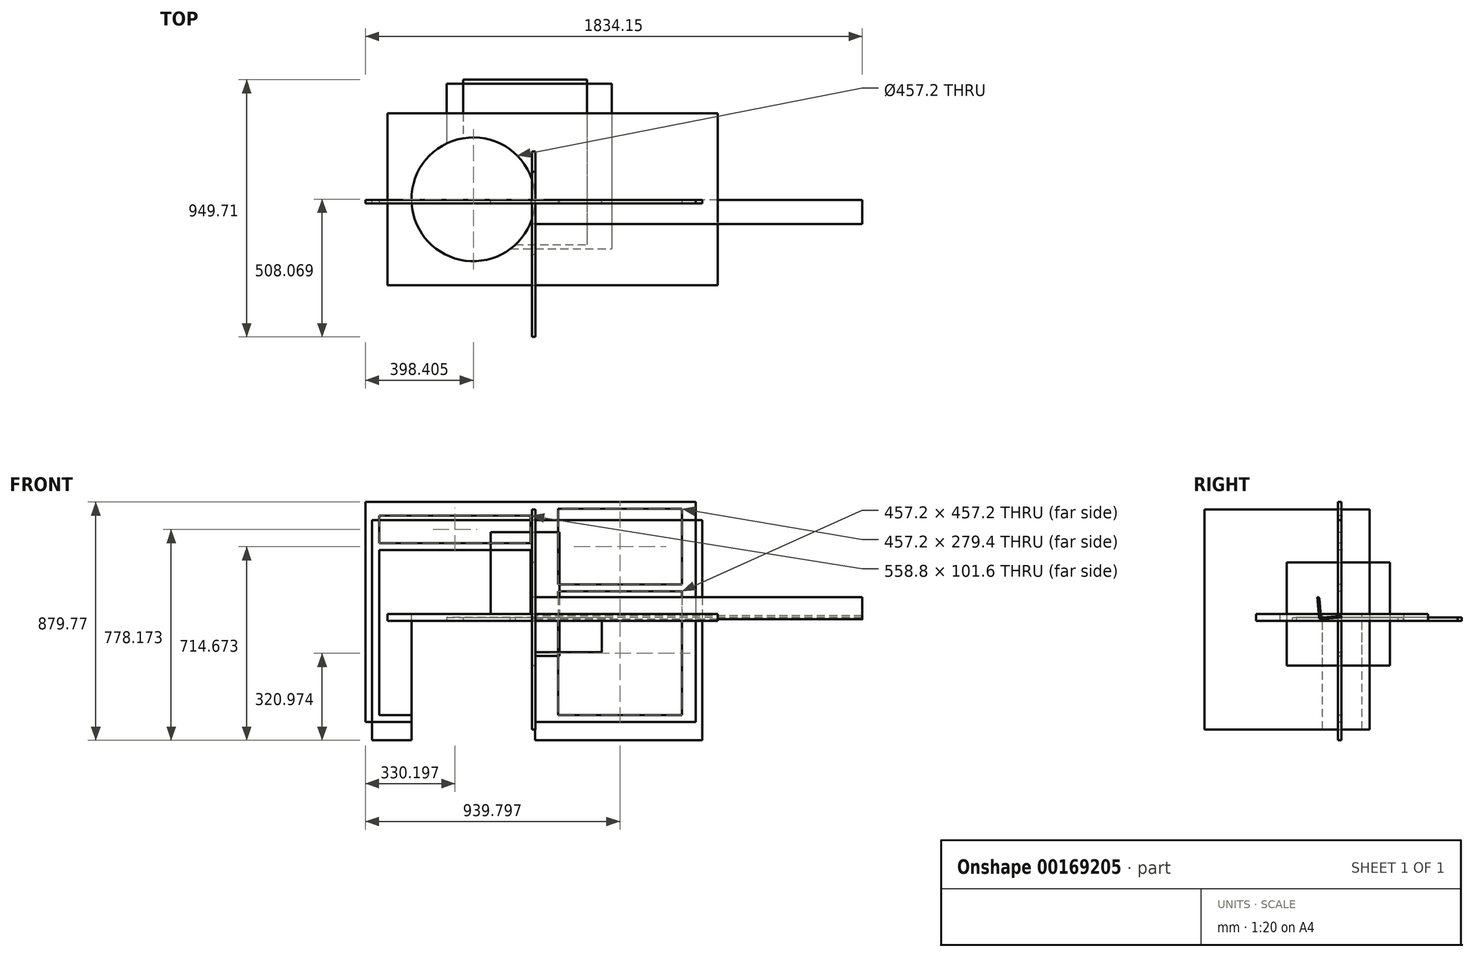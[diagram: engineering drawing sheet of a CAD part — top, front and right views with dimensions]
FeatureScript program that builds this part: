
annotation { "Feature Type Name" : "Feature", "Feature Type Description" : "" }
export const myFeature = defineFeature(function(context is Context, id is Id, definition is map)
    precondition{}
    {
        {
            var Q0;
            Q0=qCreatedBy(makeId("Front.planeOp"),FACE);
            var sketch = newSketch(context, id + "F0", { "sketchPlane" : qUnion([Q0])});
            skLineSegment(sketch, "E0.bottom", {"start": v(-614.95, 439.21) * mm, "end": v(604.25, 439.21) * mm});
            skLineSegment(sketch, "E0.top", {"start": v(-614.95, -373.59) * mm, "end": v(604.25, -373.59) * mm});
            skLineSegment(sketch, "E0.left", {"start": v(-614.95, 439.21) * mm, "end": v(-614.95, -373.59) * mm});
            skLineSegment(sketch, "E0.right", {"start": v(604.25, 439.21) * mm, "end": v(604.25, -373.59) * mm});
            skSolve(sketch);
        }
        {
            var Q0;
            Q0 = qSketchRegion(id + "F0", true);
            extrude(context, id + "F1", {"entities" : qUnion([Q0]), "depth" : 12.7 * mm});
        }
        {
            var Q0;
            Q0=makeQuery(id+"F1.opExtrude","CAP_FACE",FACE,{"disambiguationData":[OSD([sQuery(id+"F0.wireOp",EDGE,"E0.bottom"),sQuery(id+"F0.wireOp",EDGE,"E0.top"),sQuery(id+"F0.wireOp",EDGE,"E0.left"),sQuery(id+"F0.wireOp",EDGE,"E0.right")])],"isStart":false});
            var sketch = newSketch(context, id + "F2", { "sketchPlane" : qUnion([Q0])});
            skLineSegment(sketch, "E1.bottom", {"start": v(-564.15, 261.41) * mm, "end": v(-5.35, 261.41) * mm});
            skLineSegment(sketch, "E1.top", {"start": v(-564.15, -348.19) * mm, "end": v(-5.35, -348.19) * mm});
            skLineSegment(sketch, "E1.left", {"start": v(-564.15, 261.41) * mm, "end": v(-564.15, -348.19) * mm});
            skLineSegment(sketch, "E1.right", {"start": v(-5.35, 261.41) * mm, "end": v(-5.35, -348.19) * mm});
            skLineSegment(sketch, "E2.bottom", {"start": v(96.25, 109.01) * mm, "end": v(553.45, 109.01) * mm});
            skLineSegment(sketch, "E2.top", {"start": v(96.25, -348.19) * mm, "end": v(553.45, -348.19) * mm});
            skLineSegment(sketch, "E2.left", {"start": v(96.25, 109.01) * mm, "end": v(96.25, -348.19) * mm});
            skLineSegment(sketch, "E2.right", {"start": v(553.45, 109.01) * mm, "end": v(553.45, -348.19) * mm});
            skLineSegment(sketch, "E3.bottom", {"start": v(96.25, 413.81) * mm, "end": v(553.45, 413.81) * mm});
            skLineSegment(sketch, "E3.top", {"start": v(96.25, 134.41) * mm, "end": v(553.45, 134.41) * mm});
            skLineSegment(sketch, "E3.left", {"start": v(96.25, 413.81) * mm, "end": v(96.25, 134.41) * mm});
            skLineSegment(sketch, "E3.right", {"start": v(553.45, 413.81) * mm, "end": v(553.45, 134.41) * mm});
            skLineSegment(sketch, "E4.bottom", {"start": v(-564.15, 388.41) * mm, "end": v(-5.35, 388.41) * mm});
            skLineSegment(sketch, "E4.top", {"start": v(-564.15, 286.81) * mm, "end": v(-5.35, 286.81) * mm});
            skLineSegment(sketch, "E4.left", {"start": v(-564.15, 388.41) * mm, "end": v(-564.15, 286.81) * mm});
            skLineSegment(sketch, "E4.right", {"start": v(-5.35, 388.41) * mm, "end": v(-5.35, 286.81) * mm});
            skSolve(sketch);
        }
        {
            var Q0;
            Q0 = qSketchRegion(id + "F2", true);
            extrude(context, id + "F3", {"entities" : qUnion([Q0]), "operationType" : NewBodyOperationType.REMOVE, "endBound" : BoundingType.THROUGH_ALL, "oppositeDirection" : true, "depth" : 25.4 * mm});
        }
        {
            var Q0;
            Q0=qCreatedBy(makeId("Right.planeOp"),FACE);
            var sketch = newSketch(context, id + "F4", { "sketchPlane" : qUnion([Q0])});
            skLineSegment(sketch, "E5.bottom", {"start": v(-505.32, 412.33) * mm, "end": v(104.28, 412.33) * mm});
            skLineSegment(sketch, "E5.top", {"start": v(-505.32, -400.47) * mm, "end": v(104.28, -400.47) * mm});
            skLineSegment(sketch, "E5.left", {"start": v(-505.32, 412.33) * mm, "end": v(-505.32, -400.47) * mm});
            skLineSegment(sketch, "E5.right", {"start": v(104.28, 412.33) * mm, "end": v(104.28, -400.47) * mm});
            skSolve(sketch);
        }
        {
            var Q0;
            Q0 = qSketchRegion(id + "F4", true);
            extrude(context, id + "F5", {"entities" : qUnion([Q0]), "depth" : 12.7 * mm});
        }
        {
            var Q0;
            Q0=qCreatedBy(makeId("Front.planeOp"),FACE);
            var sketch = newSketch(context, id + "F6", { "sketchPlane" : qUnion([Q0])});
            skLineSegment(sketch, "E6.bottom", {"start": v(628.26, 372.24) * mm, "end": v(-590.94, 372.24) * mm});
            skLineSegment(sketch, "E6.top", {"start": v(628.26, -440.56) * mm, "end": v(-590.94, -440.56) * mm});
            skLineSegment(sketch, "E6.left", {"start": v(628.26, 372.24) * mm, "end": v(628.26, -440.56) * mm});
            skLineSegment(sketch, "E6.right", {"start": v(-590.94, 372.24) * mm, "end": v(-590.94, -440.56) * mm});
            skSolve(sketch);
        }
        {
            var Q0;
            Q0 = qSketchRegion(id + "F6", true);
            extrude(context, id + "F7", {"entities" : qUnion([Q0]), "depth" : 12.7 * mm});
        }
        {
            var Q0;
            Q0=qCreatedBy(makeId("Top.planeOp"),FACE);
            var sketch = newSketch(context, id + "F8", { "sketchPlane" : qUnion([Q0])});
            skLineSegment(sketch, "E7.bottom", {"start": v(-534.05, 320.25) * mm, "end": v(685.15, 320.25) * mm});
            skLineSegment(sketch, "E7.top", {"start": v(-534.05, -314.75) * mm, "end": v(685.15, -314.75) * mm});
            skLineSegment(sketch, "E7.left", {"start": v(-534.05, 320.25) * mm, "end": v(-534.05, -314.75) * mm});
            skLineSegment(sketch, "E7.right", {"start": v(685.15, 320.25) * mm, "end": v(685.15, -314.75) * mm});
            skSolve(sketch);
        }
        {
            var Q0;
            Q0 = qSketchRegion(id + "F8", true);
            extrude(context, id + "F9", {"entities" : qUnion([Q0]), "depth" : 25.4 * mm});
        }
        {
            var Q0;
            Q0=qCreatedBy(makeId("Top.planeOp"),FACE);
            var sketch = newSketch(context, id + "F10", { "sketchPlane" : qUnion([Q0])});
            skLineSegment(sketch, "E8.bottom", {"start": v(-315.36, 429.37) * mm, "end": v(294.24, 429.37) * mm});
            skLineSegment(sketch, "E8.top", {"start": v(-315.36, -180.23) * mm, "end": v(294.24, -180.23) * mm});
            skLineSegment(sketch, "E8.left", {"start": v(-315.36, 429.37) * mm, "end": v(-315.36, -180.23) * mm});
            skLineSegment(sketch, "E8.right", {"start": v(294.24, 429.37) * mm, "end": v(294.24, -180.23) * mm});
            skSolve(sketch);
        }
        {
            var Q0;
            Q0 = qSketchRegion(id + "F10", true);
            extrude(context, id + "F11", {"entities" : qUnion([Q0]), "depth" : 12.7 * mm});
        }
        {
            var Q0;
            Q0=qCreatedBy(makeId("Top.planeOp"),FACE);
            var sketch = newSketch(context, id + "F12", { "sketchPlane" : qUnion([Q0])});
            skLineSegment(sketch, "E9.bottom", {"start": v(-254.5, 444.4) * mm, "end": v(202.7, 444.4) * mm});
            skLineSegment(sketch, "E9.top", {"start": v(-254.5, -165.2) * mm, "end": v(202.7, -165.2) * mm});
            skLineSegment(sketch, "E9.left", {"start": v(-254.5, 444.4) * mm, "end": v(-254.5, -165.2) * mm});
            skLineSegment(sketch, "E9.right", {"start": v(202.7, 444.4) * mm, "end": v(202.7, -165.2) * mm});
            skSolve(sketch);
        }
        {
            var Q0;
            Q0 = qSketchRegion(id + "F12", true);
            extrude(context, id + "F13", {"entities" : qUnion([Q0]), "depth" : 12.7 * mm});
        }
        {
            var Q0;
            Q0=qCreatedBy(makeId("Front.planeOp"),FACE);
            var sketch = newSketch(context, id + "F14", { "sketchPlane" : qUnion([Q0])});
            skLineSegment(sketch, "E10.bottom", {"start": v(-326.1, 12.28) * mm, "end": v(258.1, 12.28) * mm});
            skLineSegment(sketch, "E10.top", {"start": v(-326.1, -114.72) * mm, "end": v(258.1, -114.72) * mm});
            skLineSegment(sketch, "E10.left", {"start": v(-326.1, 12.28) * mm, "end": v(-326.1, -114.72) * mm});
            skLineSegment(sketch, "E10.right", {"start": v(258.1, 12.28) * mm, "end": v(258.1, -114.72) * mm});
            skSolve(sketch);
        }
        {
            var Q0;
            Q0 = qSketchRegion(id + "F14", true);
            extrude(context, id + "F15", {"entities" : qUnion([Q0]), "depth" : 12.7 * mm});
        }
        {
            var Q0;
            Q0=qCreatedBy(makeId("Front.planeOp"),FACE);
            var sketch = newSketch(context, id + "F16", { "sketchPlane" : qUnion([Q0])});
            skLineSegment(sketch, "E11.bottom", {"start": v(-152.62, 328.2) * mm, "end": v(101.38, 328.2) * mm});
            skLineSegment(sketch, "E11.top", {"start": v(-152.62, -129) * mm, "end": v(101.38, -129) * mm});
            skLineSegment(sketch, "E11.left", {"start": v(-152.62, 328.2) * mm, "end": v(-152.62, -129) * mm});
            skLineSegment(sketch, "E11.right", {"start": v(101.38, 328.2) * mm, "end": v(101.38, -129) * mm});
            skSolve(sketch);
        }
        {
            var Q0;
            Q0 = qSketchRegion(id + "F16", true);
            extrude(context, id + "F17", {"entities" : qUnion([Q0]), "depth" : 12.7 * mm});
        }
        {
            var Q0;
            Q0=qCreatedBy(makeId("Right.planeOp"),FACE);
            var sketch = newSketch(context, id + "F18", { "sketchPlane" : qUnion([Q0])});
            skLineSegment(sketch, "E12", {"start": v(-81.89, 82.36) * mm, "end": v(-76.46, 19.1) * mm});
            skLineSegment(sketch, "E13", {"start": v(-69.6, 13.3) * mm, "end": v(-6.33, 18.73) * mm});
            skLineSegment(sketch, "E14.0", {"start": v(-75.38, 6.44) * mm, "end": v(0.54, 12.95) * mm});
            skLineSegment(sketch, "E14.1", {"start": v(-88.76, 88.15) * mm, "end": v(-82.25, 12.22) * mm});
            skLineSegment(sketch, "E15", {"start": v(-88.76, 88.15) * mm, "end": v(-88.76, 88.15) * mm});
            skLineSegment(sketch, "E16", {"start": v(0.54, 12.95) * mm, "end": v(0.54, 12.95) * mm});
            skPoint(sketch, "E17.visualSharp", {"position": v(-75.92, 12.77) * mm});
            skArc(sketch, "E17.filletArc", {"start": v(-76.46, 19.1) * mm, "mid": v(-74.23, 14.78) * mm, "end": v(-69.6, 13.3) * mm});
            skPoint(sketch, "E18.visualSharp", {"position": v(-81.7, 5.9) * mm});
            skArc(sketch, "E18.filletArc", {"start": v(-82.25, 12.22) * mm, "mid": v(-80.01, 7.91) * mm, "end": v(-75.38, 6.44) * mm});
            skPoint(sketch, "E19.visualSharp", {"position": v(0, 19.27) * mm});
            skArc(sketch, "E19.filletArc", {"start": v(0.54, 12.95) * mm, "mid": v(-1.7, 17.26) * mm, "end": v(-6.33, 18.73) * mm});
            skPoint(sketch, "E20.visualSharp", {"position": v(-82.43, 88.69) * mm});
            skArc(sketch, "E20.filletArc", {"start": v(-81.89, 82.36) * mm, "mid": v(-84.12, 86.68) * mm, "end": v(-88.76, 88.15) * mm});
            skSolve(sketch);
        }
        {
            var Q0;
            Q0 = qSketchRegion(id + "F18", true);
            extrude(context, id + "F19", {"entities" : qUnion([Q0]), "depth" : 1219.2 * mm});
        }
        {
            var Q0;
            Q0=qCreatedBy(makeId("Right.planeOp"),FACE);
            var sketch = newSketch(context, id + "F20", { "sketchPlane" : qUnion([Q0])});
            skLineSegment(sketch, "E21.bottom", {"start": v(-202.07, 216.05) * mm, "end": v(178.93, 216.05) * mm});
            skLineSegment(sketch, "E21.top", {"start": v(-202.07, -164.95) * mm, "end": v(178.93, -164.95) * mm});
            skLineSegment(sketch, "E21.left", {"start": v(-202.07, 216.05) * mm, "end": v(-202.07, -164.95) * mm});
            skLineSegment(sketch, "E21.right", {"start": v(178.93, 216.05) * mm, "end": v(178.93, -164.95) * mm});
            skSolve(sketch);
        }
        {
            var Q0;
            Q0 = qSketchRegion(id + "F20", true);
            extrude(context, id + "F21", {"entities" : qUnion([Q0]), "depth" : 12.7 * mm});
        }
        {
            var Q0;
            Q0=makeQuery(id+"F9.opExtrude","CAP_FACE",FACE,{"disambiguationData":[OSD([sQuery(id+"F8.wireOp",EDGE,"E7.bottom"),sQuery(id+"F8.wireOp",EDGE,"E7.top"),sQuery(id+"F8.wireOp",EDGE,"E7.left"),sQuery(id+"F8.wireOp",EDGE,"E7.right")])],"isStart":false});
            var sketch = newSketch(context, id + "F22", { "sketchPlane" : qUnion([Q0])});
            skCircle(sketch, "E22", {"center": v(-216.55, 2.75) * mm, "radius": 228.6 * mm});
            skSolve(sketch);
        }
        {
            var Q0;
            Q0 = qSketchRegion(id + "F22", true);
            extrude(context, id + "F23", {"entities" : qUnion([Q0]), "operationType" : NewBodyOperationType.REMOVE, "endBound" : BoundingType.THROUGH_ALL, "oppositeDirection" : true, "depth" : 25.4 * mm});
        }
    });
